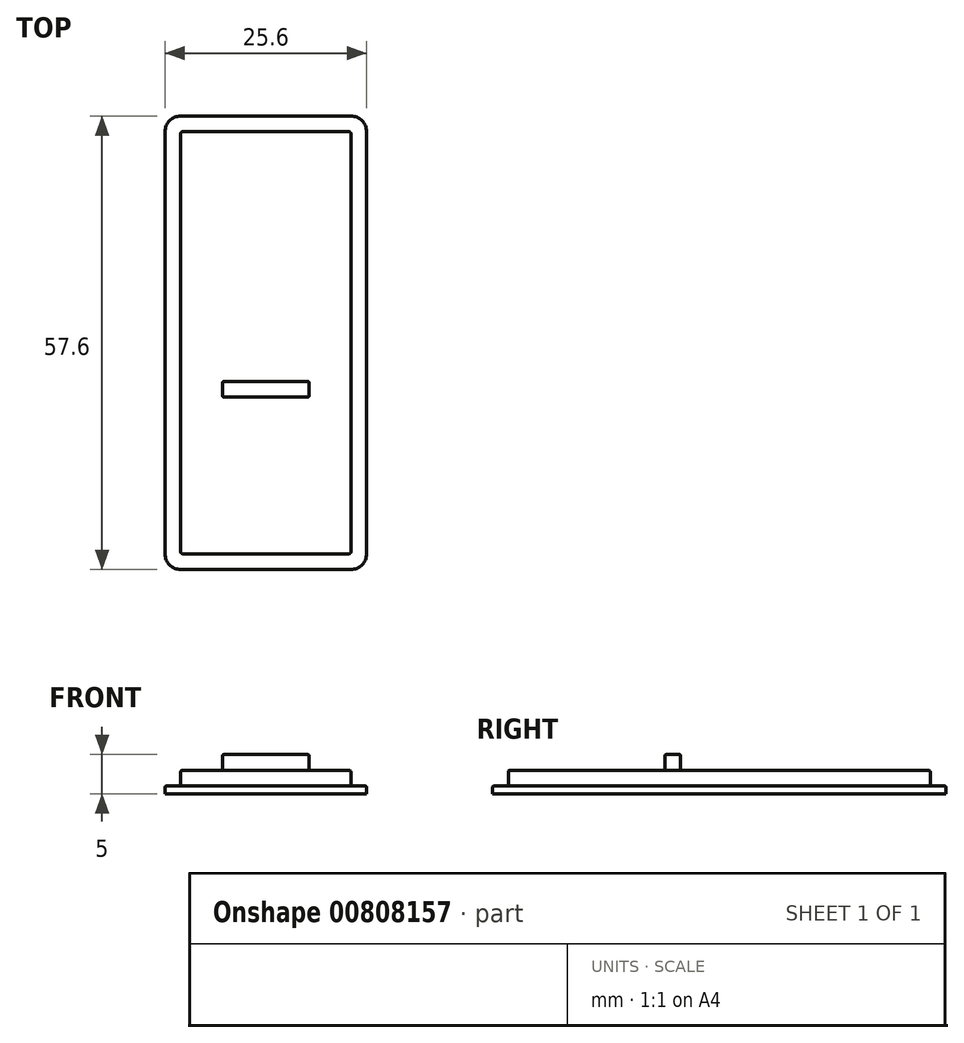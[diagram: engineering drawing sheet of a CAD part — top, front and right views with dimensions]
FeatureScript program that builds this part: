
annotation { "Feature Type Name" : "Feature", "Feature Type Description" : "" }
export const myFeature = defineFeature(function(context is Context, id is Id, definition is map)
    precondition{}
    {
        {
            var Q0;
            Q0=qCreatedBy(makeId("Top.planeOp"),FACE);
            var sketch = newSketch(context, id + "F0", { "sketchPlane" : qUnion([Q0])});
            skLineSegment(sketch, "E0.bottom", {"start": v(-11, 25.76) * mm, "end": v(11, 25.76) * mm, "construction": true});
            skLineSegment(sketch, "E0.top", {"start": v(-11, -28.24) * mm, "end": v(11, -28.24) * mm, "construction": true});
            skLineSegment(sketch, "E0.left", {"start": v(-11, 25.76) * mm, "end": v(-11, -28.24) * mm, "construction": true});
            skLineSegment(sketch, "E0.right", {"start": v(11, 25.76) * mm, "end": v(11, -28.24) * mm, "construction": true});
            skPoint(sketch, "E1", {"position": v(0, 25.76) * mm});
            skPoint(sketch, "E2", {"position": v(0, -28.24) * mm});
            skLineSegment(sketch, "E3.0", {"start": v(-12.8, 27.56) * mm, "end": v(12.8, 27.56) * mm});
            skLineSegment(sketch, "E3.1", {"start": v(-12.8, 27.56) * mm, "end": v(-12.8, -30.04) * mm});
            skLineSegment(sketch, "E3.2", {"start": v(-12.8, -30.04) * mm, "end": v(12.8, -30.04) * mm});
            skLineSegment(sketch, "E3.3", {"start": v(12.8, 27.56) * mm, "end": v(12.8, -30.04) * mm});
            skLineSegment(sketch, "E4.bottom", {"start": v(-5.5, -6.14) * mm, "end": v(5.5, -6.14) * mm});
            skLineSegment(sketch, "E4.top", {"start": v(-5.5, -8.14) * mm, "end": v(5.5, -8.14) * mm});
            skLineSegment(sketch, "E4.left", {"start": v(-5.5, -6.14) * mm, "end": v(-5.5, -8.14) * mm});
            skLineSegment(sketch, "E4.right", {"start": v(5.5, -6.14) * mm, "end": v(5.5, -8.14) * mm});
            skLineSegment(sketch, "E5.0", {"start": v(-10.8, 25.56) * mm, "end": v(-10.8, -28.04) * mm});
            skLineSegment(sketch, "E5.1", {"start": v(-10.8, 25.56) * mm, "end": v(10.8, 25.56) * mm});
            skLineSegment(sketch, "E5.2", {"start": v(10.8, 25.56) * mm, "end": v(10.8, -28.04) * mm});
            skLineSegment(sketch, "E5.3", {"start": v(-10.8, -28.04) * mm, "end": v(10.8, -28.04) * mm});
            skSolve(sketch);
        }
        {
            var Q0;
            Q0=makeQuery(id+"F0.imprint","IMPRINT",FACE,{"disambiguationData":[TD([[makeQuery(id+"F0.imprint","IMPRINT",EDGE,{"derivedFrom":sQuery(id+"F0.wireOp",EDGE,"E3.0")}),-1.0]])]});
            extrude(context, id + "F1", {"entities" : qUnion([Q0]), "depth" : 1 * mm, "offsetDistance" : 25 * mm});
        }
        {
            var Q0;
            Q0=makeQuery(id+"F0.imprint","IMPRINT",FACE,{"disambiguationData":[TD([[makeQuery(id+"F0.imprint","IMPRINT",EDGE,{"derivedFrom":sQuery(id+"F0.wireOp",EDGE,"E4.bottom")}),1.0]])]});
            extrude(context, id + "F2", {"entities" : qUnion([Q0]), "operationType" : NewBodyOperationType.ADD, "depth" : (1 + 2) * mm, "offsetDistance" : 25 * mm});
        }
        {
            var Q0;
            Q0=makeQuery(id+"F0.imprint","IMPRINT",FACE,{"disambiguationData":[TD([[makeQuery(id+"F0.imprint","IMPRINT",EDGE,{"derivedFrom":sQuery(id+"F0.wireOp",EDGE,"E4.bottom")}),-1.0]])]});
            extrude(context, id + "F3", {"entities" : qUnion([Q0]), "operationType" : NewBodyOperationType.ADD, "depth" : (1 + 2 + 2) * mm, "offsetDistance" : 25 * mm});
        }
        {
            var Q0;
            Q0=makeQuery(id+"F1.opExtrude","SWEPT_EDGE",EDGE,{"disambiguationData":[OSD([sQuery(id+"F0.wireOp",EDGE,"E3.1"),sQuery(id+"F0.wireOp",EDGE,"E3.2")])]});
            var Q1;
            Q1=makeQuery(id+"F1.opExtrude","SWEPT_EDGE",EDGE,{"disambiguationData":[OSD([sQuery(id+"F0.wireOp",EDGE,"E3.2"),sQuery(id+"F0.wireOp",EDGE,"E3.3")])]});
            var Q2;
            Q2=makeQuery(id+"F1.opExtrude","SWEPT_EDGE",EDGE,{"disambiguationData":[OSD([sQuery(id+"F0.wireOp",EDGE,"E3.0"),sQuery(id+"F0.wireOp",EDGE,"E3.3")])]});
            var Q3;
            Q3=makeQuery(id+"F1.opExtrude","SWEPT_EDGE",EDGE,{"disambiguationData":[OSD([sQuery(id+"F0.wireOp",EDGE,"E3.0"),sQuery(id+"F0.wireOp",EDGE,"E3.1")])]});
            fillet(context, id + "F4", {"entities" : qUnion([Q0, Q1, Q2, Q3]), "radius" : 2 * mm, "tangentPropagation" : true, "allowEdgeOverflow" : false});
        }
        {
            var Q0;
            Q0=makeQuery(id+"F1.opExtrude","CAP_EDGE",EDGE,{"disambiguationData":[OSD([sQuery(id+"F0.wireOp",EDGE,"E3.3")])],"isStart":false});
            var Q1;
            Q1=makeQuery(id+"F2.opExtrude","CAP_FACE",FACE,{"disambiguationData":[OSD([sQuery(id+"F0.wireOp",EDGE,"E4.bottom"),sQuery(id+"F0.wireOp",EDGE,"E4.top"),sQuery(id+"F0.wireOp",EDGE,"E4.left"),sQuery(id+"F0.wireOp",EDGE,"E4.right"),sQuery(id+"F0.wireOp",EDGE,"E5.0"),sQuery(id+"F0.wireOp",EDGE,"E5.1"),sQuery(id+"F0.wireOp",EDGE,"E5.2"),sQuery(id+"F0.wireOp",EDGE,"E5.3")])],"isStart":false});
            var Q2;
            Q2=makeQuery(id+"F2.opExtrude","SWEPT_EDGE",EDGE,{"disambiguationData":[OSD([sQuery(id+"F0.wireOp",EDGE,"E5.1"),sQuery(id+"F0.wireOp",EDGE,"E5.2")])]});
            var Q3;
            Q3=makeQuery(id+"F2.opExtrude","SWEPT_EDGE",EDGE,{"disambiguationData":[OSD([sQuery(id+"F0.wireOp",EDGE,"E5.0"),sQuery(id+"F0.wireOp",EDGE,"E5.1")])]});
            var Q4;
            Q4=makeQuery(id+"F2.opExtrude","SWEPT_EDGE",EDGE,{"disambiguationData":[OSD([sQuery(id+"F0.wireOp",EDGE,"E5.0"),sQuery(id+"F0.wireOp",EDGE,"E5.3")])]});
            var Q5;
            Q5=makeQuery(id+"F2.opExtrude","SWEPT_EDGE",EDGE,{"disambiguationData":[OSD([sQuery(id+"F0.wireOp",EDGE,"E5.2"),sQuery(id+"F0.wireOp",EDGE,"E5.3")])]});
            var Q6;
            Q6=makeQuery(id+"F3.opExtrude","CAP_FACE",FACE,{"disambiguationData":[OSD([sQuery(id+"F0.wireOp",EDGE,"E4.bottom"),sQuery(id+"F0.wireOp",EDGE,"E4.top"),sQuery(id+"F0.wireOp",EDGE,"E4.left"),sQuery(id+"F0.wireOp",EDGE,"E4.right")])],"isStart":false});
            var Q7;
            Q7=makeQuery(id+"F3.opExtrude","SWEPT_FACE",FACE,{"disambiguationData":[OSD([sQuery(id+"F0.wireOp",EDGE,"E4.top")])]});
            var Q8;
            Q8=makeQuery(id+"F3.opExtrude","SWEPT_FACE",FACE,{"disambiguationData":[OSD([sQuery(id+"F0.wireOp",EDGE,"E4.right")])]});
            var Q9;
            Q9=makeQuery(id+"F3.opExtrude","SWEPT_FACE",FACE,{"disambiguationData":[OSD([sQuery(id+"F0.wireOp",EDGE,"E4.bottom")])]});
            var Q10;
            Q10=makeQuery(id+"F3.opExtrude","SWEPT_FACE",FACE,{"disambiguationData":[OSD([sQuery(id+"F0.wireOp",EDGE,"E4.left")])]});
            fillet(context, id + "F5", {"entities" : qUnion([Q0, Q1, Q2, Q3, Q4, Q5, Q6, Q7, Q8, Q9, Q10]), "radius" : 0.2 * mm, "tangentPropagation" : true, "allowEdgeOverflow" : false});
        }
    });
